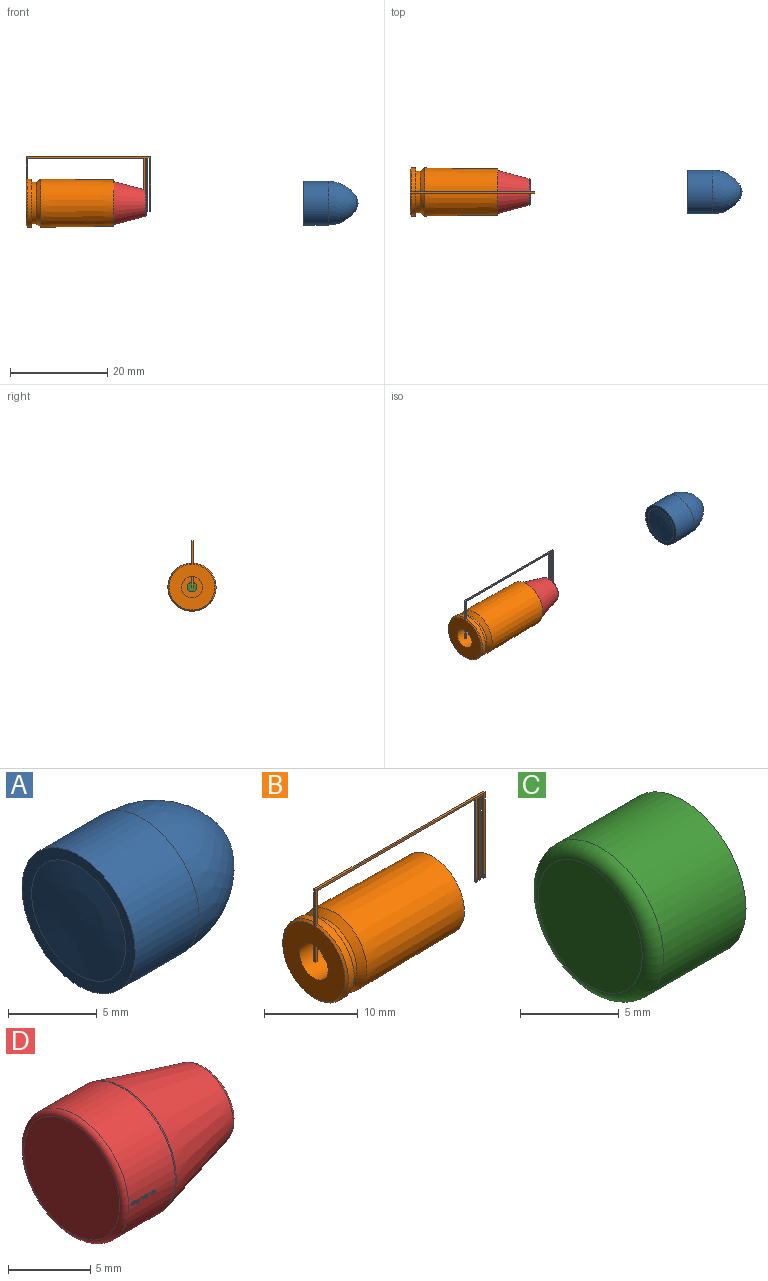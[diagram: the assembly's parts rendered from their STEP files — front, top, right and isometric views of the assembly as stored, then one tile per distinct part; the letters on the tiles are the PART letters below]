
ASSEMBLY  parts=4 mates=4
PART A: 5 faces, bbox 11.2x9x9 mm
  f0: sphere r=2.54mm, area 6.2mm2, adj f1
  f1: revolved ~9.02x9.02mm, area 146.3mm2, adj f0,f2
  f2: cylinder r=4.51mm len=9.02mm, axis (1,0,0), area 143.9mm2, adj f1,f3
  f3: plane 9.02x9.02mm, normal (-1,0,0), area 19.8mm2, adj f2,f4
  f4: sphere r=27.76mm, area 44.3mm2, adj f3
PART B: 152 faces, bbox 25.7x9.9x14.5 mm
  f0: plane 25.65x11.19mm, normal (0,-1,0), area 15.9mm2, adj f2,f3,f14,f17,f18,f19,f20,f21
  f1: plane 25.65x11.19mm, normal (0,1,0), area 15.9mm2, adj f2,f3,f14,f17,f18,f19,f20,f21
  f2: plane 0.25x0.25mm, normal (0,0,-1), area 0.1mm2, adj f0,f1,f3,f100
  f3: plane 10.93x0.25mm, normal (1,0,0), area 2.8mm2, adj f0,f1,f2,f20
  f4: cylinder r=1mm len=2mm, axis (-1,0,0), area 7mm2, adj f5,f16
  f5: plane 7.44x7.44mm, normal (1,0,0), area 40.4mm2, adj f4,f6
  f6: torus R=3.72mm, axis (-1,0,0), area 31.6mm2, adj f5,f7
  f7: cylinder r=4.48mm len=13.21mm, axis (-1,0,0), area 372mm2, adj f6,f8
  f8: plane 9.53x9.53mm, normal (1,0,0), area 8.1mm2, adj f7,f9
  f9: cone r=4.95mm half-angle=0.7deg, axis (-1,0,0), area 456.4mm2, adj f8,f10
  f10: cone r=4.32mm half-angle=35.5deg, axis (1,0,0), area 31.8mm2, adj f9,f11
  f11: cylinder r=4.32mm len=8.64mm, axis (-1,0,0), area 27.6mm2, adj f10,f12
  f12: plane 9.91x9.91mm, normal (1,0,0), area 18.5mm2, adj f11,f13
  f13: cylinder r=4.95mm len=9.91mm, axis (-1,0,0), area 27.7mm2, adj f12,f17,f22
  f14: plane 14.22x9.4mm, normal (-1,0,0), area 56.5mm2, adj f0,f1,f15,f17,f21,f24,f25,f26
  f15: cylinder r=2.16mm len=4.32mm, axis (-1,0,0), area 39.6mm2, adj f14,f16,f23,f24,f25
  f16: plane 4.32x4.32mm, normal (-1,0,0), area 11.5mm2, adj f4,f15
  f17: cone r=4.7mm half-angle=45deg, axis (1,0,0), area 10.8mm2, adj f0,f1,f13,f14
  f18: plane 24x0.25mm, normal (0,0,-1), area 6.1mm2, adj f0,f1,f19,f22
  f19: plane 10.93x0.25mm, normal (-1,0,0), area 2.8mm2, adj f0,f1,f18,f20
  f20: plane 0.25x0.25mm, normal (0,0,-1), area 0.1mm2, adj f0,f1,f3,f19
  f21: plane 25.65x0.25mm, normal (0,0,1), area 6.5mm2, adj f0,f1,f14,f73
  f22: plane 4.33x0.26mm, normal (1,0,0), area 1.1mm2, adj f0,f1,f13,f18
  f23: plane 2.16x0.25mm, normal (1,0,0), area 0.5mm2, adj f15,f24,f25,f26
  f24: plane 2.14x0.25mm, normal (0,-1,0), area 0.5mm2, adj f14,f15,f23,f26
  f25: plane 2.16x0.25mm, normal (0,1,0), area 0.5mm2, adj f14,f15,f23,f26
  f26: plane 0.25x0.25mm, normal (0,0,-1), area 0.1mm2, adj f14,f23,f24,f25
  f27: plane 0.25x0.02mm, normal (-0.66,0,-0.75), area 0mm2, adj f0,f1,f28,f35
  f28: extruded ~0.25x0.05mm, area 0mm2, adj f0,f1,f27,f29
  f29: extruded ~0.25x0.12mm, area 0mm2, adj f0,f1,f28,f30
  f30: extruded ~0.25x0.1mm, area 0mm2, adj f0,f1,f29,f31
  f31: extruded ~0.25x0.07mm, area 0mm2, adj f0,f1,f30,f32
  f32: extruded ~0.25x0.07mm, area 0mm2, adj f0,f1,f31,f33
  f33: extruded ~0.25x0.05mm, area 0mm2, adj f0,f1,f32,f34
  f34: extruded ~0.25x0.09mm, area 0mm2, adj f0,f1,f33,f35
  f35: extruded ~0.25x0.03mm, area 0mm2, adj f0,f1,f27,f34
  f36: extruded ~0.25x0.07mm, area 0mm2, adj f0,f1,f37,f50
  f37: extruded ~0.25x0.07mm, area 0mm2, adj f0,f1,f36,f38
  f38: extruded ~0.25x0.07mm, area 0mm2, adj f0,f1,f37,f39
  f39: extruded ~0.25x0.03mm, area 0mm2, adj f0,f1,f38,f40
  f40: plane 0.25x0.06mm, normal (0.09,0,1), area 0mm2, adj f0,f1,f39,f41
  f41: plane 0.25x0.08mm, normal (1,0,0), area 0mm2, adj f0,f1,f40,f42
  f42: plane 0.25x0.02mm, normal (0,0,1), area 0mm2, adj f0,f1,f41,f43
  f43: plane 0.25x0.1mm, normal (-1,0,0), area 0mm2, adj f0,f1,f42,f44
  f44: plane 0.25x0.1mm, normal (-0.07,0,-1), area 0mm2, adj f0,f1,f43,f45
  f45: plane 0.25x0.01mm, normal (0.85,0,-0.52), area 0mm2, adj f0,f1,f44,f46
  f46: extruded ~0.25x0.03mm, area 0mm2, adj f0,f1,f45,f47
  f47: extruded ~0.25x0.05mm, area 0mm2, adj f0,f1,f46,f48
  f48: extruded ~0.25x0.05mm, area 0mm2, adj f0,f1,f47,f49
  f49: extruded ~0.25x0.05mm, area 0mm2, adj f0,f1,f48,f50
  f50: plane 0.25x0.02mm, normal (-0.6,0,-0.8), area 0mm2, adj f0,f1,f36,f49
  f51: extruded ~0.25x0.07mm, area 0mm2, adj f0,f1,f52,f65
  f52: extruded ~0.25x0.07mm, area 0mm2, adj f0,f1,f51,f53
  f53: extruded ~0.25x0.07mm, area 0mm2, adj f0,f1,f52,f54
  f54: extruded ~0.25x0.03mm, area 0mm2, adj f0,f1,f53,f55
  f55: plane 0.25x0.06mm, normal (0.09,0,1), area 0mm2, adj f0,f1,f54,f56
  f56: plane 0.25x0.08mm, normal (1,0,0), area 0mm2, adj f0,f1,f55,f57
  f57: plane 0.25x0.02mm, normal (0,0,1), area 0mm2, adj f0,f1,f56,f58
  f58: plane 0.25x0.1mm, normal (-1,0,0), area 0mm2, adj f0,f1,f57,f59
  f59: plane 0.25x0.1mm, normal (-0.07,0,-1), area 0mm2, adj f0,f1,f58,f60
  f60: plane 0.25x0.01mm, normal (0.85,0,-0.52), area 0mm2, adj f0,f1,f59,f61
  f61: extruded ~0.25x0.03mm, area 0mm2, adj f0,f1,f60,f62
  f62: extruded ~0.25x0.05mm, area 0mm2, adj f0,f1,f61,f63
  f63: extruded ~0.25x0.05mm, area 0mm2, adj f0,f1,f62,f64
  f64: extruded ~0.25x0.05mm, area 0mm2, adj f0,f1,f63,f65
  f65: plane 0.25x0.02mm, normal (-0.6,0,-0.8), area 0mm2, adj f0,f1,f51,f64
  f66: extruded ~0.25x0.02mm, area 0mm2, adj f0,f1,f67,f69
  f67: extruded ~0.25x0.02mm, area 0mm2, adj f0,f1,f66,f68
  f68: extruded ~0.25x0.02mm, area 0mm2, adj f0,f1,f67,f69
  f69: extruded ~0.25x0.02mm, area 0mm2, adj f0,f1,f66,f68
  f70: plane 0.38x0.25mm, normal (0,0,-1), area 0.1mm2, adj f0,f1,f71,f99
  f71: plane 10.93x0.25mm, normal (-1,0,0), area 2.8mm2, adj f0,f1,f70,f72
  f72: plane 0.25x0.25mm, normal (0,0,-1), area 0.1mm2, adj f0,f1,f71,f73
  f73: plane 11.18x0.25mm, normal (1,0,0), area 2.8mm2, adj f0,f1,f21,f72
  f74: extruded ~0.25x0.08mm, area 0mm2, adj f0,f1,f75,f81
  f75: extruded ~0.25x0.08mm, area 0mm2, adj f0,f1,f74,f76
  f76: extruded ~0.25x0.05mm, area 0mm2, adj f0,f1,f75,f77
  f77: extruded ~0.25x0.05mm, area 0mm2, adj f0,f1,f76,f78
  f78: extruded ~0.25x0.08mm, area 0mm2, adj f0,f1,f77,f79
  f79: extruded ~0.25x0.08mm, area 0mm2, adj f0,f1,f78,f80
  f80: extruded ~0.25x0.05mm, area 0mm2, adj f0,f1,f79,f81
  f81: extruded ~0.25x0.05mm, area 0mm2, adj f0,f1,f74,f80
  f82: extruded ~0.25x0.01mm, area 0mm2, adj f0,f1,f83,f89
  f83: extruded ~0.25x0.01mm, area 0mm2, adj f0,f1,f82,f84
  f84: extruded ~0.25x0.01mm, area 0mm2, adj f0,f1,f83,f85
  f85: extruded ~0.25x0.01mm, area 0mm2, adj f0,f1,f84,f86
  f86: extruded ~0.25x0.01mm, area 0mm2, adj f0,f1,f85,f87
  f87: extruded ~0.25x0.01mm, area 0mm2, adj f0,f1,f86,f88
  f88: extruded ~0.25x0.01mm, area 0mm2, adj f0,f1,f87,f89
  f89: extruded ~0.25x0.01mm, area 0mm2, adj f0,f1,f82,f88
  f90: plane 0.25x0.02mm, normal (1,0,0), area 0mm2, adj f0,f1,f91,f98
  f91: plane 0.25x0.2mm, normal (0,0,1), area 0.1mm2, adj f0,f1,f90,f92
  f92: plane 0.25x0.02mm, normal (-1,0,0), area 0mm2, adj f0,f1,f91,f93
  f93: plane 0.25x0.05mm, normal (-0.79,0,-0.61), area 0mm2, adj f0,f1,f92,f94
  f94: plane 0.25x0.02mm, normal (0.61,0,-0.79), area 0mm2, adj f0,f1,f93,f95
  f95: extruded ~0.25x0.03mm, area 0mm2, adj f0,f1,f94,f96
  f96: extruded ~0.25x0.01mm, area 0mm2, adj f0,f1,f95,f97
  f97: extruded ~0.25x0.03mm, area 0mm2, adj f0,f1,f96,f98
  f98: plane 0.25x0.14mm, normal (0,0,-1), area 0mm2, adj f0,f1,f90,f97
  f99: plane 10.93x0.25mm, normal (1,0,0), area 2.8mm2, adj f0,f1,f70,f101
  f100: plane 10.93x0.25mm, normal (-1,0,0), area 2.8mm2, adj f0,f1,f2,f101
  f101: plane 0.25x0.25mm, normal (0,0,-1), area 0.1mm2, adj f0,f1,f99,f100
  f102: extruded ~0.25x0.12mm, area 0mm2, adj f0,f1,f103,f117
  f103: extruded ~0.25x0.05mm, area 0mm2, adj f0,f1,f102,f104
  f104: extruded ~0.25x0.03mm, area 0mm2, adj f0,f1,f103,f105
  f105: extruded ~0.25x0.04mm, area 0mm2, adj f0,f1,f104,f106
  f106: extruded ~0.25x0.05mm, area 0mm2, adj f0,f1,f105,f107
  f107: extruded ~0.25x0.05mm, area 0mm2, adj f0,f1,f106,f108
  f108: extruded ~0.25x0.04mm, area 0mm2, adj f0,f1,f107,f109
  f109: extruded ~0.25x0.04mm, area 0mm2, adj f0,f1,f108,f110
  f110: extruded ~0.25x0.03mm, area 0mm2, adj f0,f1,f109,f111
  f111: extruded ~0.25x0.02mm, area 0mm2, adj f0,f1,f110,f112
  f112: plane 0.25x0mm, normal (1,0,0), area 0mm2, adj f0,f1,f111,f113
  f113: extruded ~0.25x0.06mm, area 0mm2, adj f0,f1,f112,f114
  f114: extruded ~0.25x0.05mm, area 0mm2, adj f0,f1,f113,f115
  f115: extruded ~0.25x0.03mm, area 0mm2, adj f0,f1,f114,f116
  f116: plane 0.25x0.02mm, normal (0,0,-1), area 0mm2, adj f0,f1,f115,f117
  f117: extruded ~0.25x0.03mm, area 0mm2, adj f0,f1,f102,f116
  f118: extruded ~0.25x0.05mm, area 0mm2, adj f0,f1,f119,f136
  f119: extruded ~0.25x0.03mm, area 0mm2, adj f0,f1,f118,f120
  f120: plane 0.25x0.06mm, normal (0.08,0,1), area 0mm2, adj f0,f1,f119,f121
  f121: plane 0.25x0.08mm, normal (1,0,0), area 0mm2, adj f0,f1,f120,f122
  f122: plane 0.25x0.02mm, normal (0,0,1), area 0mm2, adj f0,f1,f121,f123
  f123: plane 0.25x0.1mm, normal (-1,0,0), area 0mm2, adj f0,f1,f122,f124
  f124: plane 0.25x0.09mm, normal (-0.08,0,-1), area 0mm2, adj f0,f1,f123,f125
  f125: plane 0.25x0.01mm, normal (0.84,0,-0.54), area 0mm2, adj f0,f1,f124,f126
  f126: extruded ~0.25x0.04mm, area 0mm2, adj f0,f1,f125,f127
  f127: extruded ~0.25x0.05mm, area 0mm2, adj f0,f1,f126,f128
  f128: extruded ~0.25x0.03mm, area 0mm2, adj f0,f1,f127,f129
  f129: extruded ~0.25x0.04mm, area 0mm2, adj f0,f1,f128,f130
  f130: extruded ~0.25x0.03mm, area 0mm2, adj f0,f1,f129,f131
  f131: extruded ~0.25x0.02mm, area 0mm2, adj f0,f1,f130,f132
  f132: plane 0.25x0.02mm, normal (0,0,-1), area 0mm2, adj f0,f1,f131,f133
  f133: extruded ~0.25x0.05mm, area 0mm2, adj f0,f1,f132,f134
  f134: extruded ~0.25x0.06mm, area 0mm2, adj f0,f1,f133,f135
  f135: extruded ~0.25x0.05mm, area 0mm2, adj f0,f1,f134,f136
  f136: extruded ~0.25x0.04mm, area 0mm2, adj f0,f1,f118,f135
  f137: plane 0.25x0.18mm, normal (-0.42,0,-0.91), area 0.1mm2, adj f0,f1,f138,f143
  f138: plane 0.25x0.03mm, normal (1,0,0), area 0mm2, adj f0,f1,f137,f139
  f139: plane 0.25x0.18mm, normal (0.41,0,0.91), area 0.1mm2, adj f0,f1,f138,f140
  f140: plane 0.25x0.02mm, normal (0,0,1), area 0mm2, adj f0,f1,f139,f141
  f141: plane 0.25x0.13mm, normal (-1,0,0), area 0mm2, adj f0,f1,f140,f142
  f142: plane 0.25x0.02mm, normal (0,0,-1), area 0mm2, adj f0,f1,f141,f143
  f143: plane 0.25x0.11mm, normal (1,0,0), area 0mm2, adj f0,f1,f137,f142
  f144: extruded ~0.25x0.01mm, area 0mm2, adj f0,f1,f145,f151
  f145: extruded ~0.25x0.01mm, area 0mm2, adj f0,f1,f144,f146
  f146: extruded ~0.25x0.01mm, area 0mm2, adj f0,f1,f145,f147
  f147: extruded ~0.25x0.01mm, area 0mm2, adj f0,f1,f146,f148
  f148: extruded ~0.25x0.01mm, area 0mm2, adj f0,f1,f147,f149
  f149: extruded ~0.25x0.01mm, area 0mm2, adj f0,f1,f148,f150
  f150: extruded ~0.25x0.01mm, area 0mm2, adj f0,f1,f149,f151
  f151: extruded ~0.25x0.01mm, area 0mm2, adj f0,f1,f144,f150
PART C: 4 faces, bbox 6.7x9.7x9.7 mm
  f0: cylinder r=4.48mm len=8.97mm, axis (1,0,0), area 166.7mm2, adj f1,f3
  f1: torus R=3.72mm, axis (1,0,0), area 31.6mm2, adj f0,f2
  f2: plane 7.44x7.44mm, normal (-1,0,0), area 43.5mm2, adj f1
  f3: plane 8.97x8.97mm, normal (1,0,0), area 63.1mm2, adj f0
PART D: 239 faces, bbox 11.4x9.8x9.8 mm
  f0: cylinder r=4.51mm len=9.02mm, axis (1,0,0), area 113.5mm2, adj f1,f9,f10,f11,f12,f13,f14,f15
  f1: torus R=4.13mm, axis (1,0,0), area 16.4mm2, adj f0,f2
  f2: plane 8.26x8.26mm, normal (-1,0,0), area 53.5mm2, adj f1
  f3: plane 2.03x2.03mm, normal (1,0,0), area 3.2mm2, adj f4
  f4: cone r=1.24mm half-angle=4.2deg, axis (1,0,0), area 21.9mm2, adj f3,f5
  f5: torus R=1.62mm, axis (1,0,0), area 5mm2, adj f4,f6
  f6: plane 4.75x4.75mm, normal (1,0,0), area 9.4mm2, adj f5,f7
  f7: torus R=2.37mm, axis (1,0,0), area 8.1mm2, adj f6,f8
  f8: cone r=4.5mm half-angle=14.8deg, axis (-1,0,0), area 156.5mm2, adj f7,f9
  f9: torus R=4.13mm, axis (1,0,0), area 2.8mm2, adj f0,f8
  f10: extruded ~2.54x0.02mm, area 0.1mm2, adj f0,f11,f22,f23
  f11: extruded ~2.54x0.03mm, area 0.1mm2, adj f0,f10,f12,f23
  f12: extruded ~2.54x0.03mm, area 0.1mm2, adj f0,f11,f13,f23
  f13: plane 2.54x0mm, normal (0,0,-1), area 0mm2, adj f0,f12,f14,f23
  f14: plane 2.54x0.04mm, normal (-1,0,-0.09), area 0.1mm2, adj f0,f13,f15,f23
  f15: plane 2.54x0.02mm, normal (0,0,-1), area 0.1mm2, adj f0,f14,f16,f23
  f16: plane 2.54x0.19mm, normal (1,0,0), area 0.5mm2, adj f0,f15,f17,f23
  f17: plane 2.54x0.03mm, normal (0,0,1), area 0.1mm2, adj f0,f16,f18,f23
  f18: plane 2.54x0.1mm, normal (-1,0,0), area 0.3mm2, adj f0,f17,f19,f23
  f19: extruded ~2.54x0.05mm, area 0.1mm2, adj f0,f18,f20,f23
  f20: extruded ~2.54x0.04mm, area 0.1mm2, adj f0,f19,f21,f23
  f21: extruded ~2.54x0.02mm, area 0.1mm2, adj f0,f20,f22,f23
  f22: plane 2.54x0.03mm, normal (-0.99,0,0.15), area 0.1mm2, adj f0,f10,f21,f23
  f23: plane 0.19x0.11mm, normal (0,-1,0), area 0mm2, adj f10,f11,f12,f13,f14,f15,f16,f17
  f24: extruded ~2.54x0.03mm, area 0.1mm2, adj f25,f67,f68,f234
  f25: extruded ~2.54x0.03mm, area 0.1mm2, adj f24,f26,f68,f234
  f26: extruded ~2.54x0.03mm, area 0.1mm2, adj f25,f27,f68,f234
  f27: extruded ~2.54x0.04mm, area 0.2mm2, adj f26,f28,f68,f234
  f28: extruded ~2.54x0.04mm, area 0.2mm2, adj f27,f67,f68,f234
  f29: extruded ~2.54x0.02mm, area 0.1mm2, adj f30,f65,f68,f69
  f30: extruded ~2.54x0.03mm, area 0.1mm2, adj f29,f31,f68,f69
  f31: extruded ~2.54x0.03mm, area 0.1mm2, adj f30,f32,f68,f69
  f32: plane 2.54x0.03mm, normal (0,0,1), area 0.1mm2, adj f31,f33,f68,f69
  f33: extruded ~2.54x0.04mm, area 0.1mm2, adj f32,f34,f68,f69
  f34: extruded ~2.54x0.02mm, area 0.1mm2, adj f33,f35,f68,f69
  f35: extruded ~2.54x0.03mm, area 0.1mm2, adj f34,f36,f68,f69
  f36: extruded ~2.54x0.05mm, area 0.1mm2, adj f35,f65,f68,f69
  f37: plane 2.54x0.02mm, normal (-1,0,0), area 0mm2, adj f0,f38,f66,f68
  f38: plane 2.54x0.07mm, normal (0,0,-1), area 0.2mm2, adj f0,f37,f39,f68
  f39: extruded ~2.54x0.03mm, area 0.1mm2, adj f0,f38,f40,f68
  f40: extruded ~2.54x0.05mm, area 0.1mm2, adj f0,f39,f41,f68
  f41: extruded ~2.54x0.05mm, area 0.1mm2, adj f0,f40,f42,f68
  f42: extruded ~2.54x0.03mm, area 0.1mm2, adj f0,f41,f43,f68
  f43: extruded ~2.54x0.02mm, area 0.1mm2, adj f0,f42,f44,f68
  f44: extruded ~2.54x0.02mm, area 0.1mm2, adj f0,f43,f45,f68
  f45: extruded ~2.54x0.02mm, area 0mm2, adj f0,f44,f46,f68
  f46: extruded ~2.54x0.02mm, area 0mm2, adj f0,f45,f47,f68
  f47: extruded ~2.54x0.01mm, area 0mm2, adj f0,f46,f48,f68
  f48: extruded ~2.54x0.03mm, area 0.1mm2, adj f0,f47,f49,f68
  f49: extruded ~2.54x0.03mm, area 0.1mm2, adj f0,f48,f50,f68
  f50: extruded ~2.54x0.04mm, area 0.1mm2, adj f0,f49,f51,f68
  f51: extruded ~2.54x0.06mm, area 0.2mm2, adj f0,f50,f52,f68
  f52: extruded ~2.54x0.07mm, area 0.2mm2, adj f0,f51,f53,f68
  f53: extruded ~2.54x0.05mm, area 0.1mm2, adj f0,f52,f54,f68
  f54: extruded ~2.54x0.04mm, area 0.1mm2, adj f0,f53,f55,f68
  f55: extruded ~2.54x0.05mm, area 0.1mm2, adj f0,f54,f56,f68
  f56: plane 2.54x0.03mm, normal (0,0,-1), area 0.1mm2, adj f0,f55,f57,f68
  f57: extruded ~2.54x0.02mm, area 0.1mm2, adj f0,f56,f58,f68
  f58: extruded ~2.54x0.01mm, area 0mm2, adj f0,f57,f59,f68
  f59: extruded ~2.54x0.02mm, area 0.1mm2, adj f0,f58,f60,f68
  f60: extruded ~2.54x0.02mm, area 0mm2, adj f0,f59,f61,f68
  f61: extruded ~2.54x0.05mm, area 0.1mm2, adj f0,f60,f62,f68
  f62: extruded ~2.54x0.04mm, area 0.1mm2, adj f0,f61,f63,f68
  f63: extruded ~2.54x0.02mm, area 0.1mm2, adj f0,f62,f64,f68
  f64: extruded ~2.54x0.02mm, area 0mm2, adj f0,f63,f66,f68
  f65: extruded ~2.54x0.04mm, area 0.1mm2, adj f29,f36,f68,f69
  f66: plane 2.54x0.04mm, normal (-0.12,0,0.99), area 0.1mm2, adj f0,f37,f64,f68
  f67: extruded ~2.54x0.03mm, area 0.1mm2, adj f24,f28,f68,f234
  f68: plane 0.28x0.18mm, normal (0,-1,0), area 0mm2, adj f24,f25,f26,f27,f28,f29,f30,f31
  f69: cylinder r=4.51mm len=0.12mm, axis (1,0,0), area 0mm2, adj f29,f30,f31,f32,f33,f34,f35,f36
  f70: plane 2.54x0.12mm, normal (1,0,0), area 0.3mm2, adj f0,f71,f87,f88
  f71: plane 2.54x0.03mm, normal (0,0,1), area 0.1mm2, adj f0,f70,f72,f88
  f72: plane 2.54x0.12mm, normal (-1,0,0), area 0.3mm2, adj f0,f71,f73,f88
  f73: extruded ~2.54x0.05mm, area 0.1mm2, adj f0,f72,f74,f88
  f74: extruded ~2.54x0.05mm, area 0.1mm2, adj f0,f73,f75,f88
  f75: extruded ~2.54x0.04mm, area 0.1mm2, adj f0,f74,f76,f88
  f76: extruded ~2.54x0.02mm, area 0.1mm2, adj f0,f75,f77,f88
  f77: plane 2.54x0mm, normal (0,0,-1), area 0mm2, adj f0,f76,f78,f88
  f78: extruded ~2.54x0.02mm, area 0.1mm2, adj f0,f77,f79,f88
  f79: plane 2.54x0.08mm, normal (-1,0,0), area 0.2mm2, adj f0,f78,f80,f88
  f80: plane 2.54x0.03mm, normal (0,0,-1), area 0.1mm2, adj f0,f79,f81,f88
  f81: plane 2.54x0.27mm, normal (1,0,0), area 0.7mm2, adj f0,f80,f82,f88
  f82: plane 2.54x0.03mm, normal (0,0,1), area 0.1mm2, adj f0,f81,f83,f88
  f83: plane 2.54x0.1mm, normal (-1,0,0), area 0.3mm2, adj f0,f82,f84,f88
  f84: extruded ~2.54x0.05mm, area 0.1mm2, adj f0,f83,f85,f88
  f85: extruded ~2.54x0.04mm, area 0.1mm2, adj f0,f84,f86,f88
  f86: extruded ~2.54x0.03mm, area 0.1mm2, adj f0,f85,f87,f88
  f87: extruded ~2.54x0.03mm, area 0.1mm2, adj f0,f70,f86,f88
  f88: plane 0.27x0.16mm, normal (0,-1,0), area 0mm2, adj f70,f71,f72,f73,f74,f75,f76,f77
  f89: plane 2.54x0.03mm, normal (0,0,-1), area 0.1mm2, adj f0,f90,f104,f105
  f90: plane 2.54x0.19mm, normal (0.93,0,0.37), area 0.5mm2, adj f0,f89,f91,f105
  f91: plane 2.54x0.03mm, normal (0.93,0,-0.37), area 0.1mm2, adj f0,f90,f92,f105
  f92: extruded ~2.54x0.04mm, area 0.1mm2, adj f0,f91,f93,f105
  f93: extruded ~2.54x0.02mm, area 0.1mm2, adj f0,f92,f94,f105
  f94: plane 2.54x0.02mm, normal (1,0,0), area 0.1mm2, adj f0,f93,f95,f105
  f95: extruded ~2.54x0.03mm, area 0.1mm2, adj f0,f94,f96,f105
  f96: extruded ~2.54x0.04mm, area 0.1mm2, adj f0,f95,f97,f105
  f97: extruded ~2.54x0.05mm, area 0.1mm2, adj f0,f96,f98,f105
  f98: plane 2.54x0.22mm, normal (-0.94,0,0.35), area 0.6mm2, adj f0,f97,f99,f105
  f99: plane 2.54x0.03mm, normal (0,0,-1), area 0.1mm2, adj f0,f98,f100,f105
  f100: extruded ~2.54x0.13mm, area 0.4mm2, adj f0,f99,f101,f105
  f101: extruded ~2.54x0.03mm, area 0.1mm2, adj f0,f100,f102,f105
  f102: plane 2.54x0mm, normal (0,0,-1), area 0mm2, adj f0,f101,f103,f105
  f103: extruded ~2.54x0.05mm, area 0.1mm2, adj f0,f102,f104,f105
  f104: plane 2.54x0.11mm, normal (-0.93,0,-0.36), area 0.3mm2, adj f0,f89,f103,f105
  f105: plane 0.27x0.18mm, normal (0,-1,0), area 0mm2, adj f89,f90,f91,f92,f93,f94,f95,f96
  f106: extruded ~2.54x0.02mm, area 0mm2, adj f0,f107,f124,f125
  f107: extruded ~2.54x0.02mm, area 0.1mm2, adj f0,f106,f108,f125
  f108: extruded ~2.54x0.03mm, area 0.1mm2, adj f0,f107,f109,f125
  f109: plane 2.54x0.11mm, normal (-1,0,0), area 0.3mm2, adj f0,f108,f110,f125
  f110: plane 2.54x0.05mm, normal (0,0,1), area 0.1mm2, adj f0,f109,f111,f125
  f111: plane 2.54x0.02mm, normal (-1,0,0), area 0.1mm2, adj f0,f110,f112,f125
  f112: plane 2.54x0.05mm, normal (0,0,-1), area 0.1mm2, adj f0,f111,f113,f125
  f113: plane 2.54x0.04mm, normal (-1,0,0), area 0.1mm2, adj f0,f112,f114,f125
  f114: plane 2.54x0.02mm, normal (0,0,-1), area 0mm2, adj f0,f113,f115,f125
  f115: plane 2.54x0.04mm, normal (0.96,0,-0.29), area 0.1mm2, adj f0,f114,f116,f125
  f116: plane 2.54x0.03mm, normal (0.4,0,-0.92), area 0.1mm2, adj f0,f115,f117,f125
  f117: plane 2.54x0.01mm, normal (1,0,0), area 0mm2, adj f0,f116,f118,f125
  f118: plane 2.54x0.03mm, normal (0,0,1), area 0.1mm2, adj f0,f117,f119,f125
  f119: plane 2.54x0.11mm, normal (1,0,0), area 0.3mm2, adj f0,f118,f120,f125
  f120: extruded ~2.54x0.06mm, area 0.2mm2, adj f0,f119,f121,f125
  f121: extruded ~2.54x0.02mm, area 0mm2, adj f0,f120,f122,f125
  f122: extruded ~2.54x0.01mm, area 0mm2, adj f0,f121,f123,f125
  f123: plane 2.54x0.02mm, normal (-1,0,0), area 0.1mm2, adj f0,f122,f124,f125
  f124: extruded ~2.54x0.01mm, area 0mm2, adj f0,f106,f123,f125
  f125: plane 0.24x0.11mm, normal (0,-1,0), area 0mm2, adj f106,f107,f108,f109,f110,f111,f112,f113
  f126: extruded ~2.54x0.04mm, area 0.1mm2, adj f127,f148,f152,f235
  f127: extruded ~2.54x0.03mm, area 0.1mm2, adj f126,f128,f152,f235
  f128: extruded ~2.54x0.02mm, area 0.1mm2, adj f127,f129,f152,f235
  f129: extruded ~2.54x0.03mm, area 0.1mm2, adj f128,f130,f152,f235
  f130: extruded ~2.54x0.02mm, area 0.1mm2, adj f129,f131,f152,f235
  f131: extruded ~2.54x0.02mm, area 0.1mm2, adj f130,f149,f152,f235
  f132: extruded ~2.54x0.04mm, area 0.1mm2, adj f148,f150,f152,f235
  f133: extruded ~2.54x0.15mm, area 0.5mm2, adj f0,f134,f147,f152
  f134: extruded ~2.54x0.06mm, area 0.2mm2, adj f0,f133,f135,f152
  f135: extruded ~2.54x0.04mm, area 0.1mm2, adj f0,f134,f136,f152
  f136: extruded ~2.54x0.05mm, area 0.1mm2, adj f0,f135,f137,f152
  f137: extruded ~2.54x0.06mm, area 0.2mm2, adj f0,f136,f138,f152
  f138: extruded ~2.54x0.06mm, area 0.2mm2, adj f0,f137,f139,f152
  f139: extruded ~2.54x0.06mm, area 0.2mm2, adj f0,f138,f140,f152
  f140: extruded ~2.54x0.05mm, area 0.1mm2, adj f0,f139,f141,f152
  f141: extruded ~2.54x0.04mm, area 0.1mm2, adj f0,f140,f142,f152
  f142: extruded ~2.54x0.03mm, area 0.1mm2, adj f0,f141,f151,f152
  f143: extruded ~2.54x0.08mm, area 0.2mm2, adj f0,f144,f151,f152
  f144: extruded ~2.54x0.06mm, area 0.2mm2, adj f0,f143,f145,f152
  f145: extruded ~2.54x0.03mm, area 0.1mm2, adj f0,f144,f146,f152
  f146: plane 2.54x0.03mm, normal (1,0,0), area 0.1mm2, adj f0,f145,f147,f152
  f147: extruded ~2.54x0.03mm, area 0.1mm2, adj f0,f133,f146,f152
  f148: extruded ~2.54x0.04mm, area 0.1mm2, adj f126,f132,f152,f235
  f149: extruded ~2.54x0.03mm, area 0.1mm2, adj f131,f150,f152,f235
  f150: extruded ~2.54x0.04mm, area 0.1mm2, adj f132,f149,f152,f235
  f151: plane 2.54x0mm, normal (0,0,1), area 0mm2, adj f0,f142,f143,f152
  f152: plane 0.26x0.17mm, normal (0,-1,0), area 0mm2, adj f126,f127,f128,f129,f130,f131,f132,f133
  f153: extruded ~2.54x0.08mm, area 0.2mm2, adj f154,f166,f169,f236
  f154: extruded ~2.54x0.08mm, area 0.2mm2, adj f153,f155,f169,f236
  f155: extruded ~2.54x0.04mm, area 0.1mm2, adj f154,f156,f169,f236
  f156: extruded ~2.54x0.04mm, area 0.1mm2, adj f155,f157,f169,f236
  f157: extruded ~2.54x0.08mm, area 0.2mm2, adj f156,f158,f169,f236
  f158: extruded ~2.54x0.08mm, area 0.2mm2, adj f157,f159,f169,f236
  f159: extruded ~2.54x0.04mm, area 0.1mm2, adj f158,f166,f169,f236
  f160: extruded ~2.54x0.06mm, area 0.2mm2, adj f0,f161,f168,f169
  f161: extruded ~2.54x0.06mm, area 0.2mm2, adj f0,f160,f162,f169
  f162: extruded ~2.54x0.1mm, area 0.3mm2, adj f0,f161,f163,f169
  f163: extruded ~2.54x0.1mm, area 0.3mm2, adj f0,f162,f164,f169
  f164: extruded ~2.54x0.06mm, area 0.2mm2, adj f0,f163,f165,f169
  f165: extruded ~2.54x0.06mm, area 0.2mm2, adj f0,f164,f167,f169
  f166: extruded ~2.54x0.04mm, area 0.1mm2, adj f153,f159,f169,f236
  f167: extruded ~2.54x0.1mm, area 0.3mm2, adj f0,f165,f168,f169
  f168: extruded ~2.54x0.1mm, area 0.3mm2, adj f0,f160,f167,f169
  f169: plane 0.26x0.17mm, normal (0,-1,0), area 0mm2, adj f153,f154,f155,f156,f157,f158,f159,f160
  f170: extruded ~2.54x0.04mm, area 0.1mm2, adj f171,f193,f194,f237
  f171: extruded ~2.54x0.04mm, area 0.1mm2, adj f170,f172,f194,f237
  f172: extruded ~2.54x0.05mm, area 0.1mm2, adj f171,f173,f194,f237
  f173: extruded ~2.54x0.06mm, area 0.1mm2, adj f172,f174,f194,f237
  f174: extruded ~2.54x0.04mm, area 0.1mm2, adj f173,f175,f194,f237
  f175: extruded ~2.54x0.04mm, area 0.1mm2, adj f174,f176,f194,f237
  f176: extruded ~2.54x0.06mm, area 0.2mm2, adj f175,f177,f194,f237
  f177: plane 2.54x0.01mm, normal (1,0,0), area 0mm2, adj f176,f193,f194,f237
  f178: plane 2.54x0mm, normal (0,0,1), area 0mm2, adj f0,f179,f192,f194
  f179: plane 2.54x0.03mm, normal (0.99,0,0.15), area 0.1mm2, adj f0,f178,f180,f194
  f180: plane 2.54x0.02mm, normal (0,0,1), area 0.1mm2, adj f0,f179,f181,f194
  f181: plane 2.54x0.27mm, normal (-1,0,0), area 0.7mm2, adj f0,f180,f182,f194
  f182: plane 2.54x0.03mm, normal (0,0,-1), area 0.1mm2, adj f0,f181,f183,f194
  f183: plane 2.54x0.08mm, normal (1,0,0), area 0.2mm2, adj f0,f182,f184,f194
  f184: plane 2.54x0.01mm, normal (1,0,0.05), area 0mm2, adj f0,f183,f185,f194
  f185: plane 2.54x0.01mm, normal (1,0,0.09), area 0mm2, adj f0,f184,f186,f194
  f186: plane 2.54x0mm, normal (0,0,-1), area 0mm2, adj f0,f185,f187,f194
  f187: extruded ~2.54x0.06mm, area 0.2mm2, adj f0,f186,f188,f194
  f188: extruded ~2.54x0.06mm, area 0.2mm2, adj f0,f187,f189,f194
  f189: extruded ~2.54x0.07mm, area 0.2mm2, adj f0,f188,f190,f194
  f190: extruded ~2.54x0.07mm, area 0.2mm2, adj f0,f189,f191,f194
  f191: extruded ~2.54x0.06mm, area 0.2mm2, adj f0,f190,f192,f194
  f192: extruded ~2.54x0.06mm, area 0.2mm2, adj f0,f178,f191,f194
  f193: extruded ~2.54x0.05mm, area 0.1mm2, adj f170,f177,f194,f237
  f194: plane 0.27x0.17mm, normal (0,-1,0), area 0mm2, adj f170,f171,f172,f173,f174,f175,f176,f177
  f195: extruded ~2.54x0.04mm, area 0.1mm2, adj f196,f219,f220,f238
  f196: extruded ~2.54x0.04mm, area 0.1mm2, adj f195,f197,f220,f238
  f197: extruded ~2.54x0.05mm, area 0.1mm2, adj f196,f198,f220,f238
  f198: extruded ~2.54x0.05mm, area 0.1mm2, adj f197,f199,f220,f238
  f199: extruded ~2.54x0.04mm, area 0.1mm2, adj f198,f200,f220,f238
  f200: extruded ~2.54x0.04mm, area 0.1mm2, adj f199,f201,f220,f238
  f201: extruded ~2.54x0.06mm, area 0.2mm2, adj f200,f202,f220,f238
  f202: plane 2.54x0.01mm, normal (-1,0,0), area 0mm2, adj f201,f219,f220,f238
  f203: extruded ~2.54x0.03mm, area 0.1mm2, adj f0,f204,f218,f220
  f204: extruded ~2.54x0.06mm, area 0.2mm2, adj f0,f203,f205,f220
  f205: extruded ~2.54x0.07mm, area 0.2mm2, adj f0,f204,f206,f220
  f206: extruded ~2.54x0.07mm, area 0.2mm2, adj f0,f205,f207,f220
  f207: extruded ~2.54x0.06mm, area 0.2mm2, adj f0,f206,f208,f220
  f208: extruded ~2.54x0.03mm, area 0.1mm2, adj f0,f207,f209,f220
  f209: extruded ~2.54x0.03mm, area 0.1mm2, adj f0,f208,f210,f220
  f210: plane 2.54x0mm, normal (0,0,-1), area 0mm2, adj f0,f209,f211,f220
  f211: plane 2.54x0.03mm, normal (-0.99,0,-0.15), area 0.1mm2, adj f0,f210,f212,f220
  f212: plane 2.54x0.02mm, normal (0,0,-1), area 0.1mm2, adj f0,f211,f213,f220
  f213: plane 2.54x0.27mm, normal (1,0,0), area 0.7mm2, adj f0,f212,f214,f220
  f214: plane 2.54x0.03mm, normal (0,0,1), area 0.1mm2, adj f0,f213,f215,f220
  f215: plane 2.54x0.08mm, normal (-1,0,0), area 0.2mm2, adj f0,f214,f216,f220
  f216: extruded ~2.54x0.03mm, area 0.1mm2, adj f0,f215,f217,f220
  f217: plane 2.54x0mm, normal (0,0,1), area 0mm2, adj f0,f216,f218,f220
  f218: extruded ~2.54x0.03mm, area 0.1mm2, adj f0,f203,f217,f220
  f219: extruded ~2.54x0.05mm, area 0.1mm2, adj f195,f202,f220,f238
  f220: plane 0.28x0.17mm, normal (0,-1,0), area 0mm2, adj f195,f196,f197,f198,f199,f200,f201,f202
  f221: plane 2.54x0.09mm, normal (0.81,0,0.58), area 0.3mm2, adj f0,f222,f232,f233
  f222: plane 2.54x0.1mm, normal (0.81,0,-0.58), area 0.3mm2, adj f0,f221,f223,f233
  f223: plane 2.54x0.04mm, normal (0,0,1), area 0.1mm2, adj f0,f222,f224,f233
  f224: plane 2.54x0.08mm, normal (-0.82,0,0.57), area 0.2mm2, adj f0,f223,f225,f233
  f225: plane 2.54x0.08mm, normal (0.82,0,0.57), area 0.2mm2, adj f0,f224,f226,f233
  f226: plane 2.54x0.04mm, normal (0,0,1), area 0.1mm2, adj f0,f225,f227,f233
  f227: plane 2.54x0.1mm, normal (-0.81,0,-0.58), area 0.3mm2, adj f0,f226,f228,f233
  f228: plane 2.54x0.09mm, normal (-0.81,0,0.58), area 0.3mm2, adj f0,f227,f229,f233
  f229: plane 2.54x0.03mm, normal (0,0,-1), area 0.1mm2, adj f0,f228,f230,f233
  f230: plane 2.54x0.07mm, normal (0.82,0,-0.57), area 0.2mm2, adj f0,f229,f231,f233
  f231: plane 2.54x0.07mm, normal (-0.82,0,-0.57), area 0.2mm2, adj f0,f230,f232,f233
  f232: plane 2.54x0.03mm, normal (0,0,-1), area 0.1mm2, adj f0,f221,f231,f233
  f233: plane 0.19x0.17mm, normal (0,-1,0), area 0mm2, adj f221,f222,f223,f224,f225,f226,f227,f228
  f234: cylinder r=4.51mm len=0.08mm, axis (1,0,0), area 0mm2, adj f24,f25,f26,f27,f28,f67
  f235: cylinder r=4.51mm len=0.11mm, axis (1,0,0), area 0mm2, adj f126,f127,f128,f129,f130,f131,f132,f148
  f236: cylinder r=4.51mm len=0.21mm, axis (1,0,0), area 0mm2, adj f153,f154,f155,f156,f157,f158,f159,f166
  f237: cylinder r=4.51mm len=0.15mm, axis (1,0,0), area 0mm2, adj f170,f171,f172,f173,f174,f175,f176,f177
  f238: cylinder r=4.51mm len=0.15mm, axis (1,0,0), area 0mm2, adj f195,f196,f197,f198,f199,f200,f201,f202
PLACE A rot(axis=(-1,0,0),152.6deg) t=(65.66,0,9.33)mm
PLACE B t=(8.55,0,9.33)mm fixed
PLACE C t=(8.55,0,9.33)mm
PLACE D rot(axis=(-1,0,0),0.5deg) t=(21.88,0,9.33)mm
MATE cylindrical C.f0 <-> B.f4  axis (-1,0,0) through (12.58,0,9.33)mm
MATE planar C.f0 <-> B.f4  axis (-1,0,0) through (12.58,0,9.33)mm
MATE cylindrical D.f0 <-> C.f0  axis (-1,0,0) through (21.88,0,9.33)mm
MATE cylindrical A.f2 <-> B.f4  axis (-1,0,0) through (65.66,0,9.33)mm
